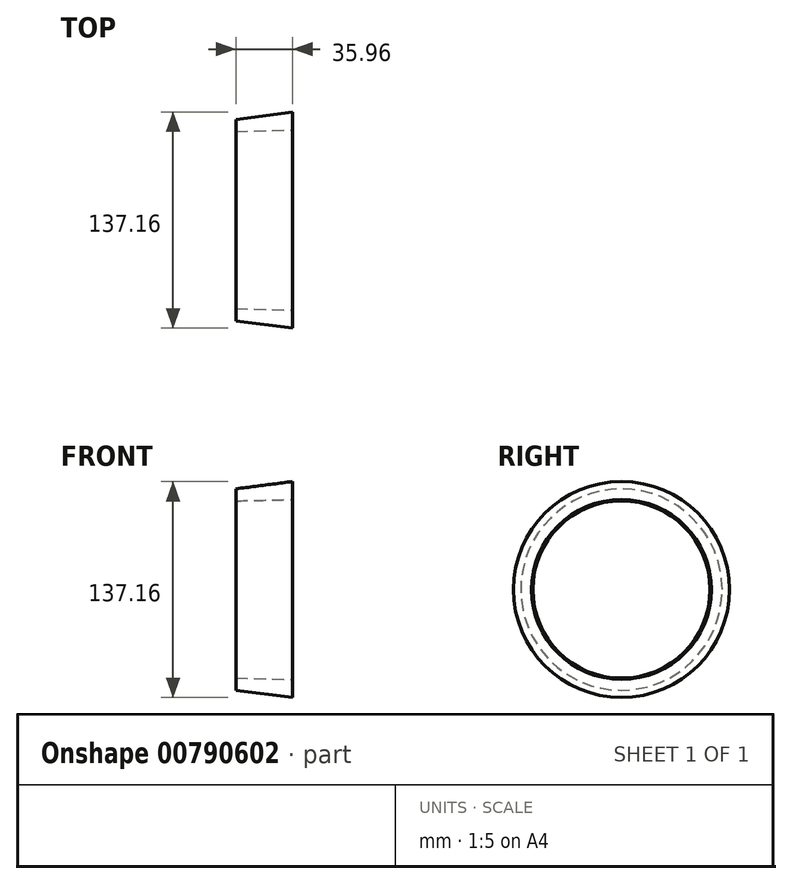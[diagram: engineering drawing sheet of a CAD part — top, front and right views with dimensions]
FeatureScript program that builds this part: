
annotation { "Feature Type Name" : "Feature", "Feature Type Description" : "" }
export const myFeature = defineFeature(function(context is Context, id is Id, definition is map)
    precondition{}
    {
        {
            var Q0;
            Q0=qCreatedBy(makeId("Right.planeOp"),FACE);
            var sketch = newSketch(context, id + "F0", { "sketchPlane" : qUnion([Q0])});
            skCircle(sketch, "E0", {"center": v(0, 0) * mm, "radius": 57.15 * mm});
            skCircle(sketch, "E1", {"center": v(0, 0) * mm, "radius": 63.5 * mm});
            skSolve(sketch);
        }
        {
            var Q0;
            Q0=qCreatedBy(makeId("Front.planeOp"),FACE);
            var sketch = newSketch(context, id + "F1", { "sketchPlane" : qUnion([Q0])});
            skLineSegment(sketch, "E2", {"start": v(0, 63.96) * mm, "end": v(35.96, 68.58) * mm});
            skLineSegment(sketch, "E3", {"start": v(35.96, 68.58) * mm, "end": v(35.96, 57.15) * mm});
            skLineSegment(sketch, "E4", {"start": v(35.96, 57.15) * mm, "end": v(0, 56.3) * mm});
            skLineSegment(sketch, "E5", {"start": v(0, 56.3) * mm, "end": v(0, 63.96) * mm});
            skLineSegment(sketch, "E6", {"start": v(0, 0) * mm, "end": v(46.43, 0) * mm});
            skSolve(sketch);
        }
        {
            var Q0;
            Q0=makeQuery(id+"F1.imprint","IMPRINT",FACE,{"disambiguationData":[TD([[makeQuery(id+"F1.imprint","IMPRINT",EDGE,{"derivedFrom":sQuery(id+"F1.wireOp",EDGE,"E2")}),-1.0]])]});
            var Q1;
            Q1=sQuery(id+"F1.wireOp",EDGE,"E6");
            revolve(context, id + "F2", {"surfaceOperationType" : NewSurfaceOperationType.NEW, "entities" : qUnion([Q0]), "axis" : qUnion([Q1]), "revolveType" : RevolveType.FULL});
        }
    });
